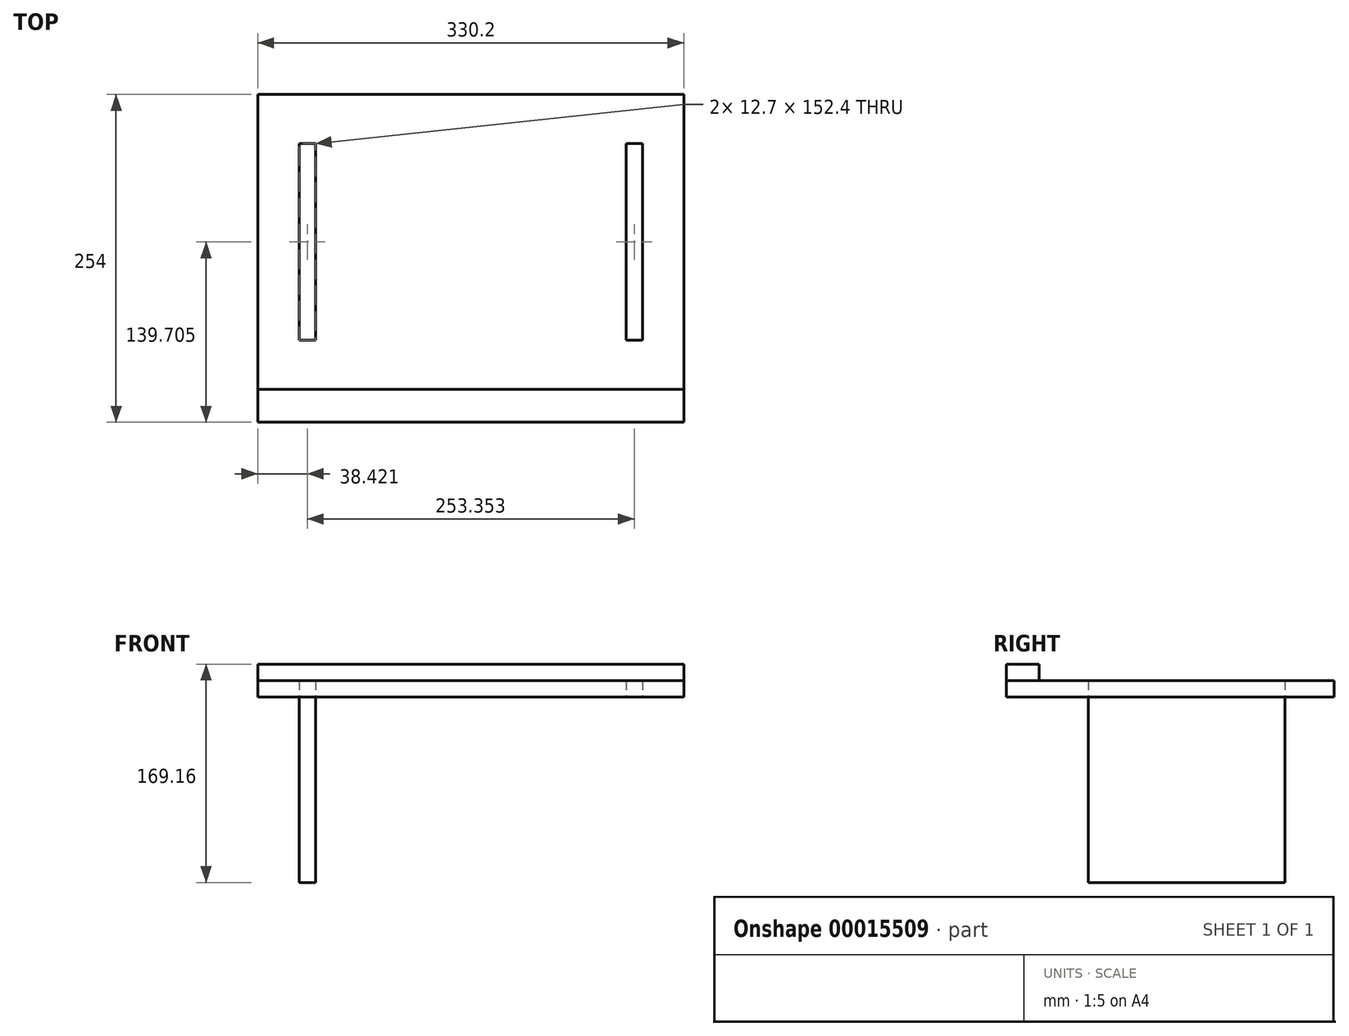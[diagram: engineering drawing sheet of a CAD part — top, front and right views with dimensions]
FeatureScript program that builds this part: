
annotation { "Feature Type Name" : "Feature", "Feature Type Description" : "" }
export const myFeature = defineFeature(function(context is Context, id is Id, definition is map)
    precondition{}
    {
        {
            var Q0;
            Q0=qCreatedBy(makeId("Top.planeOp"),FACE);
            var sketch = newSketch(context, id + "F0", { "sketchPlane" : qUnion([Q0])});
            skLineSegment(sketch, "E0.bottom", {"start": v(-144.83, 100.67) * mm, "end": v(185.37, 100.67) * mm});
            skLineSegment(sketch, "E0.top", {"start": v(-144.83, -153.33) * mm, "end": v(185.37, -153.33) * mm});
            skLineSegment(sketch, "E0.left", {"start": v(-144.83, 100.67) * mm, "end": v(-144.83, -153.33) * mm});
            skLineSegment(sketch, "E0.right", {"start": v(185.37, 100.67) * mm, "end": v(185.37, -153.33) * mm});
            skLineSegment(sketch, "E1.bottom", {"start": v(-112.76, 62.57) * mm, "end": v(-100.06, 62.57) * mm});
            skLineSegment(sketch, "E1.top", {"start": v(-112.76, -89.83) * mm, "end": v(-100.06, -89.83) * mm});
            skLineSegment(sketch, "E1.left", {"start": v(-112.76, 62.57) * mm, "end": v(-112.76, -89.83) * mm});
            skLineSegment(sketch, "E1.right", {"start": v(-100.06, 62.57) * mm, "end": v(-100.06, -89.83) * mm});
            skLineSegment(sketch, "E2", {"start": v(20.27, 100.67) * mm, "end": v(20.27, -153.33) * mm, "construction": true});
            skLineSegment(sketch, "E3.MirrorCS", {"start": v(140.6, 62.57) * mm, "end": v(140.6, -89.83) * mm});
            skLineSegment(sketch, "E4.MirrorCS", {"start": v(153.3, -89.83) * mm, "end": v(140.6, -89.83) * mm});
            skLineSegment(sketch, "E5.MirrorCS", {"start": v(153.3, 62.57) * mm, "end": v(153.3, -89.83) * mm});
            skLineSegment(sketch, "E6.MirrorCS", {"start": v(153.3, 62.57) * mm, "end": v(140.6, 62.57) * mm});
            skSolve(sketch);
        }
        {
            var Q0;
            Q0=makeQuery(id+"F0.imprint","IMPRINT",FACE,{"disambiguationData":[TD([[makeQuery(id+"F0.imprint","IMPRINT",EDGE,{"derivedFrom":sQuery(id+"F0.wireOp",EDGE,"E0.bottom")}),-1.0]])]});
            extrude(context, id + "F1", {"entities" : qUnion([Q0]), "depth" : 12.7 * mm});
        }
        {
            var Q0;
            Q0=makeQuery(id+"F1.opExtrude","CAP_FACE",FACE,{"disambiguationData":[OSD([sQuery(id+"F0.wireOp",EDGE,"E0.bottom"),sQuery(id+"F0.wireOp",EDGE,"E0.top"),sQuery(id+"F0.wireOp",EDGE,"E0.left"),sQuery(id+"F0.wireOp",EDGE,"E0.right"),sQuery(id+"F0.wireOp",EDGE,"E1.bottom"),sQuery(id+"F0.wireOp",EDGE,"E1.top"),sQuery(id+"F0.wireOp",EDGE,"E1.left"),sQuery(id+"F0.wireOp",EDGE,"E1.right"),sQuery(id+"F0.wireOp",EDGE,"E3.MirrorCS"),sQuery(id+"F0.wireOp",EDGE,"E4.MirrorCS"),sQuery(id+"F0.wireOp",EDGE,"E5.MirrorCS"),sQuery(id+"F0.wireOp",EDGE,"E6.MirrorCS")])],"isStart":false});
            var sketch = newSketch(context, id + "F2", { "sketchPlane" : qUnion([Q0])});
            skLineSegment(sketch, "E7.0", {"start": v(-144.83, -127.93) * mm, "end": v(185.37, -127.93) * mm});
            skLineSegment(sketch, "E8.1", {"start": v(-144.83, 100.67) * mm, "end": v(-144.83, -153.33) * mm});
            skLineSegment(sketch, "E8.2", {"start": v(-144.83, -153.33) * mm, "end": v(185.37, -153.33) * mm});
            skLineSegment(sketch, "E8.3", {"start": v(185.37, 100.67) * mm, "end": v(185.37, -153.33) * mm});
            skLineSegment(sketch, "E8.4", {"start": v(-144.83, 100.67) * mm, "end": v(185.37, 100.67) * mm});
            skSolve(sketch);
        }
        {
            var Q0;
            {var subQ1=sQuery(id+"F2.wireOp",EDGE,"E7.0");Q0=makeQuery(id+"F2.imprint","IMPRINT",FACE,{"disambiguationData":[TD([[makeQuery(id+"F2.imprint","IMPRINT",EDGE,{"derivedFrom":subQ1}),-1.0]])]});}
            var Q1;
            Q1=sQuery(id+"F2.wireOp",EDGE,"E8.2");
            var Q2;
            Q2=sQuery(id+"F2.wireOp",EDGE,"E8.1");
            var Q3;
            Q3=sQuery(id+"F2.wireOp",EDGE,"E7.0");
            var Q4;
            Q4=sQuery(id+"F2.wireOp",EDGE,"E8.3");
            extrude(context, id + "F3", {"entities" : qUnion([Q0]), "surfaceEntities" : qUnion([Q1, Q2, Q3, Q4]), "depth" : 12.7 * mm});
        }
        {
            var Q0;
            Q0=makeQuery(id+"F1.opExtrude","CAP_FACE",FACE,{"disambiguationData":[OSD([sQuery(id+"F0.wireOp",EDGE,"E0.bottom"),sQuery(id+"F0.wireOp",EDGE,"E0.top"),sQuery(id+"F0.wireOp",EDGE,"E0.left"),sQuery(id+"F0.wireOp",EDGE,"E0.right"),sQuery(id+"F0.wireOp",EDGE,"E1.bottom"),sQuery(id+"F0.wireOp",EDGE,"E1.top"),sQuery(id+"F0.wireOp",EDGE,"E1.left"),sQuery(id+"F0.wireOp",EDGE,"E1.right"),sQuery(id+"F0.wireOp",EDGE,"E3.MirrorCS"),sQuery(id+"F0.wireOp",EDGE,"E4.MirrorCS"),sQuery(id+"F0.wireOp",EDGE,"E5.MirrorCS"),sQuery(id+"F0.wireOp",EDGE,"E6.MirrorCS")])],"isStart":true});
            var sketch = newSketch(context, id + "F4", { "sketchPlane" : qUnion([Q0])});
            skSolve(sketch);
        }
        {
            var Q0;
            Q0=makeQuery(id+"F4.imprint","IMPRINT",FACE,{"disambiguationData":[TD([[makeQuery(id+"F4.imprint","IMPRINT",EDGE,{"derivedFrom":makeQuery(id+"F1.opExtrude","CAP_EDGE",EDGE,{"disambiguationData":[OSD([sQuery(id+"F0.wireOp",EDGE,"E1.bottom")])],"isStart":true})}),1.0]])]});
            extrude(context, id + "F5", {"entities" : qUnion([Q0]), "depth" : 143.76 * mm});
        }
    });
